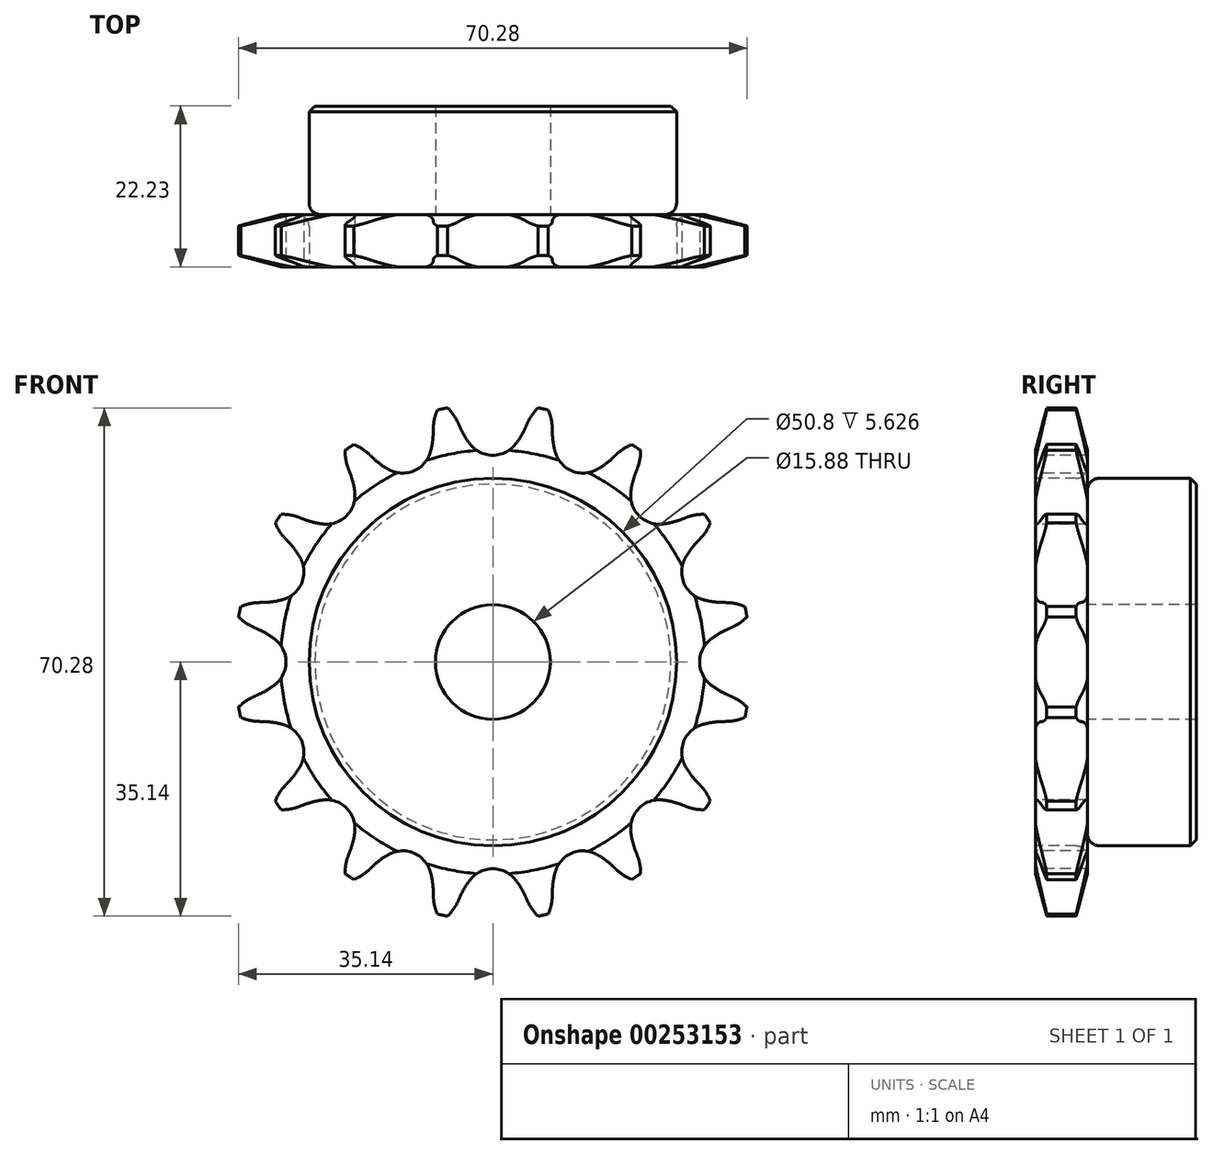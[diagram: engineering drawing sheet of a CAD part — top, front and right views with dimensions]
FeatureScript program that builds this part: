
annotation { "Feature Type Name" : "Feature", "Feature Type Description" : "" }
export const myFeature = defineFeature(function(context is Context, id is Id, definition is map)
    precondition{}
    {
        {
            var Q0;
            Q0=qCreatedBy(makeId("Right.planeOp"),FACE);
            var sketch = newSketch(context, id + "F0", { "sketchPlane" : qUnion([Q0])});
            skLineSegment(sketch, "E0", {"start": v(0, 0) * mm, "end": v(22.23, 0) * mm, "construction": true});
            skLineSegment(sketch, "E1.bottom", {"start": v(0, 7.94) * mm, "end": v(7.21, 7.94) * mm});
            skLineSegment(sketch, "E1.top", {"start": v(0, 35.69) * mm, "end": v(7.21, 35.69) * mm});
            skLineSegment(sketch, "E1.left", {"start": v(0, 7.94) * mm, "end": v(0, 35.69) * mm});
            skLineSegment(sketch, "E1.right", {"start": v(7.21, 7.94) * mm, "end": v(7.21, 35.69) * mm});
            skLineSegment(sketch, "E2.bottom", {"start": v(0, 7.94) * mm, "end": v(22.23, 7.94) * mm});
            skLineSegment(sketch, "E2.top", {"start": v(0, 25.4) * mm, "end": v(22.23, 25.4) * mm});
            skLineSegment(sketch, "E2.left", {"start": v(0, 7.94) * mm, "end": v(0, 25.4) * mm});
            skLineSegment(sketch, "E2.right", {"start": v(22.23, 7.94) * mm, "end": v(22.23, 25.4) * mm});
            skLineSegment(sketch, "E3.MirrorCS", {"start": v(0, -7.94) * mm, "end": v(7.21, -7.94) * mm});
            skLineSegment(sketch, "E4.MirrorCS", {"start": v(22.23, -7.94) * mm, "end": v(22.23, -25.4) * mm});
            skLineSegment(sketch, "E5.MirrorCS", {"start": v(0, -7.94) * mm, "end": v(0, -25.4) * mm});
            skLineSegment(sketch, "E6.MirrorCS", {"start": v(0, -35.69) * mm, "end": v(7.21, -35.69) * mm});
            skLineSegment(sketch, "E7.MirrorCS", {"start": v(0, -7.94) * mm, "end": v(0, -35.69) * mm});
            skLineSegment(sketch, "E8.MirrorCS", {"start": v(7.21, -7.94) * mm, "end": v(7.21, -35.69) * mm});
            skLineSegment(sketch, "E9.MirrorCS", {"start": v(0, -7.94) * mm, "end": v(22.23, -7.94) * mm});
            skLineSegment(sketch, "E10.MirrorCS", {"start": v(0, -25.4) * mm, "end": v(22.23, -25.4) * mm});
            skSolve(sketch);
        }
        {
            var Q0;
            {var subQ5=sQuery(id+"F0.wireOp",EDGE,"E2.right");Q0=makeQuery(id+"F0.imprint","IMPRINT",FACE,{"disambiguationData":[TD([[makeQuery(id+"F0.imprint","IMPRINT",EDGE,{"derivedFrom":subQ5}),1.0]])]});}
            var Q1;
            {var subQ5=sQuery(id+"F0.wireOp",EDGE,"E2.left");Q1=makeQuery(id+"F0.imprint","IMPRINT",FACE,{"disambiguationData":[TD([[makeQuery(id+"F0.imprint","IMPRINT",EDGE,{"derivedFrom":subQ5}),-1.0]])]});}
            var Q2;
            {var subQ0=sQuery(id+"F0.wireOp",EDGE,"E1.top");Q2=makeQuery(id+"F0.imprint","IMPRINT",FACE,{"disambiguationData":[TD([[makeQuery(id+"F0.imprint","IMPRINT",EDGE,{"derivedFrom":subQ0}),-1.0]])]});}
            var Q3;
            Q3=sQuery(id+"F0.wireOp",EDGE,"E0");
            revolve(context, id + "F1", {"entities" : qUnion([Q0, Q1, Q2]), "axis" : qUnion([Q3]), "revolveType" : RevolveType.FULL});
        }
        {
            var Q0;
            Q0=makeQuery(id+"F1.opRevolve","SWEPT_EDGE",EDGE,{"disambiguationData":[OSD([sQuery(id+"F0.wireOp",EDGE,"E1.right"),sQuery(id+"F0.wireOp",EDGE,"E2.top")])]});
            fillet(context, id + "F2", {"entities" : qUnion([Q0]), "radius" : 1.59 * mm, "tangentPropagation" : true, "allowEdgeOverflow" : false});
        }
        {
            var Q0;
            Q0=makeQuery(id+"F1.opRevolve","SWEPT_EDGE",EDGE,{"disambiguationData":[OSD([sQuery(id+"F0.wireOp",EDGE,"E2.top"),sQuery(id+"F0.wireOp",EDGE,"E2.right")])]});
            chamfer(context, id + "F3", {"entities" : qUnion([Q0]), "width" : 0.8 * mm, "tangentPropagation" : true});
        }
        {
            var Q0;
            Q0=makeQuery(id+"F1.opRevolve","SWEPT_EDGE",EDGE,{"disambiguationData":[OSD([sQuery(id+"F0.wireOp",EDGE,"E1.top"),sQuery(id+"F0.wireOp",EDGE,"E1.left")])]});
            var Q1;
            Q1=makeQuery(id+"F1.opRevolve","SWEPT_EDGE",EDGE,{"disambiguationData":[OSD([sQuery(id+"F0.wireOp",EDGE,"E1.top"),sQuery(id+"F0.wireOp",EDGE,"E1.right")])]});
            chamfer(context, id + "F4", {"entities" : qUnion([Q0, Q1]), "chamferType" : ChamferType.TWO_OFFSETS, "width1" : 6.35 * mm, "oppositeDirection" : false, "width2" : 1.57 * mm, "tangentPropagation" : true});
        }
        {
            var Q0;
            Q0=qCreatedBy(makeId("Front.planeOp"),FACE);
            var sketch = newSketch(context, id + "F5", { "sketchPlane" : qUnion([Q0])});
            skCircle(sketch, "E11", {"center": v(0, 0) * mm, "radius": 32.55 * mm, "construction": true});
            skLineSegment(sketch, "E12", {"start": v(0, 0) * mm, "end": v(0, 32.55) * mm, "construction": true});
            skLineSegment(sketch, "E13", {"start": v(29.08, 32.55) * mm, "end": v(0, 32.55) * mm, "construction": true});
            skLineSegment(sketch, "E14", {"start": v(0, 32.55) * mm, "end": v(5, 36.56) * mm, "construction": true});
            skLineSegment(sketch, "E15", {"start": v(5, 36.56) * mm, "end": v(-4.46, 32.3) * mm, "construction": true});
            skLineSegment(sketch, "E16", {"start": v(3.63, 14.35) * mm, "end": v(-4.46, 32.3) * mm, "construction": true});
            skLineSegment(sketch, "E17", {"start": v(0, 0) * mm, "end": v(-7.13, 35.85) * mm, "construction": true});
            skArc(sketch, "E18", {"start": v(-7.13, 35.85) * mm, "mid": v(-15.87, 26.15) * mm, "end": v(-4.82, 33.1) * mm, "construction": true});
            skArc(sketch, "E19", {"start": v(-4.82, 33.1) * mm, "mid": v(-5.78, 34.63) * mm, "end": v(-7.13, 35.85) * mm});
            skArc(sketch, "E20", {"start": v(-4.46, 32.3) * mm, "mid": v(-3.84, 31.14) * mm, "end": v(-3.1, 30.07) * mm});
            skLineSegment(sketch, "E21", {"start": v(-3.1, 30.07) * mm, "end": v(-3.1, 30.07) * mm});
            skArc(sketch, "E22.MirrorCS", {"start": v(4.46, 32.3) * mm, "mid": v(3.84, 31.14) * mm, "end": v(3.1, 30.07) * mm});
            skArc(sketch, "E23.MirrorCS", {"start": v(4.82, 33.1) * mm, "mid": v(5.78, 34.63) * mm, "end": v(7.13, 35.85) * mm});
            skLineSegment(sketch, "E24", {"start": v(4.82, 33.1) * mm, "end": v(4.46, 32.3) * mm});
            skLineSegment(sketch, "E25", {"start": v(3.1, 30.07) * mm, "end": v(3.1, 30.07) * mm});
            skArc(sketch, "E26", {"start": v(-3.1, 30.07) * mm, "mid": v(13.83, 41.97) * mm, "end": v(-4.46, 32.3) * mm, "construction": true});
            skArc(sketch, "E27", {"start": v(3.1, 30.07) * mm, "mid": v(0, 36.51) * mm, "end": v(-3.1, 30.07) * mm, "construction": true});
            skArc(sketch, "E28", {"start": v(-3.1, 30.07) * mm, "mid": v(0, 28.59) * mm, "end": v(3.1, 30.07) * mm});
            skLineSegment(sketch, "E29", {"start": v(-4.82, 33.1) * mm, "end": v(-4.46, 32.3) * mm});
            skArc(sketch, "E30.1.0", {"start": v(-17.12, 28.74) * mm, "mid": v(-18.6, 29.79) * mm, "end": v(-20.3, 30.4) * mm});
            skArc(sketch, "E30.1.1", {"start": v(-16.48, 28.14) * mm, "mid": v(-15.47, 27.3) * mm, "end": v(-14.36, 26.6) * mm});
            skArc(sketch, "E30.1.2", {"start": v(-14.36, 26.6) * mm, "mid": v(-10.94, 26.41) * mm, "end": v(-8.65, 28.96) * mm});
            skArc(sketch, "E30.1.3", {"start": v(-8.24, 31.55) * mm, "mid": v(-8.37, 30.24) * mm, "end": v(-8.65, 28.96) * mm});
            skLineSegment(sketch, "E30.1.4", {"start": v(-8.22, 32.42) * mm, "end": v(-8.24, 31.55) * mm});
            skArc(sketch, "E30.1.5", {"start": v(-8.22, 32.42) * mm, "mid": v(-7.91, 34.21) * mm, "end": v(-7.13, 35.85) * mm});
            skLineSegment(sketch, "E30.1.6", {"start": v(-17.12, 28.74) * mm, "end": v(-16.48, 28.14) * mm});
            skArc(sketch, "E30.2.0", {"start": v(-26.8, 20) * mm, "mid": v(-28.58, 20.4) * mm, "end": v(-30.4, 20.3) * mm});
            skArc(sketch, "E30.2.1", {"start": v(-26, 19.69) * mm, "mid": v(-24.74, 19.3) * mm, "end": v(-23.45, 19.08) * mm});
            skArc(sketch, "E30.2.2", {"start": v(-23.45, 19.08) * mm, "mid": v(-20.21, 20.21) * mm, "end": v(-19.08, 23.45) * mm});
            skArc(sketch, "E30.2.3", {"start": v(-19.69, 26) * mm, "mid": v(-19.3, 24.74) * mm, "end": v(-19.08, 23.45) * mm});
            skLineSegment(sketch, "E30.2.4", {"start": v(-20, 26.8) * mm, "end": v(-19.69, 26) * mm});
            skArc(sketch, "E30.2.5", {"start": v(-20, 26.8) * mm, "mid": v(-20.4, 28.58) * mm, "end": v(-20.3, 30.4) * mm});
            skLineSegment(sketch, "E30.2.6", {"start": v(-26.8, 20) * mm, "end": v(-26, 19.69) * mm});
            skArc(sketch, "E30.3.0", {"start": v(-32.42, 8.22) * mm, "mid": v(-34.21, 7.91) * mm, "end": v(-35.85, 7.13) * mm});
            skArc(sketch, "E30.3.1", {"start": v(-31.55, 8.24) * mm, "mid": v(-30.24, 8.37) * mm, "end": v(-28.96, 8.65) * mm});
            skArc(sketch, "E30.3.2", {"start": v(-28.96, 8.65) * mm, "mid": v(-26.41, 10.94) * mm, "end": v(-26.6, 14.36) * mm});
            skArc(sketch, "E30.3.3", {"start": v(-28.14, 16.48) * mm, "mid": v(-27.3, 15.47) * mm, "end": v(-26.6, 14.36) * mm});
            skLineSegment(sketch, "E30.3.4", {"start": v(-28.74, 17.12) * mm, "end": v(-28.14, 16.48) * mm});
            skArc(sketch, "E30.3.5", {"start": v(-28.74, 17.12) * mm, "mid": v(-29.79, 18.6) * mm, "end": v(-30.4, 20.3) * mm});
            skLineSegment(sketch, "E30.3.6", {"start": v(-32.42, 8.22) * mm, "end": v(-31.55, 8.24) * mm});
            skArc(sketch, "E30.4.0", {"start": v(-33.1, -4.82) * mm, "mid": v(-34.63, -5.78) * mm, "end": v(-35.85, -7.13) * mm});
            skArc(sketch, "E30.4.1", {"start": v(-32.3, -4.46) * mm, "mid": v(-31.14, -3.84) * mm, "end": v(-30.07, -3.1) * mm});
            skArc(sketch, "E30.4.2", {"start": v(-30.07, -3.1) * mm, "mid": v(-28.59, 0) * mm, "end": v(-30.07, 3.1) * mm});
            skArc(sketch, "E30.4.3", {"start": v(-32.3, 4.46) * mm, "mid": v(-31.14, 3.84) * mm, "end": v(-30.07, 3.1) * mm});
            skLineSegment(sketch, "E30.4.4", {"start": v(-33.1, 4.82) * mm, "end": v(-32.3, 4.46) * mm});
            skArc(sketch, "E30.4.5", {"start": v(-33.1, 4.82) * mm, "mid": v(-34.63, 5.78) * mm, "end": v(-35.85, 7.13) * mm});
            skLineSegment(sketch, "E30.4.6", {"start": v(-33.1, -4.82) * mm, "end": v(-32.3, -4.46) * mm});
            skArc(sketch, "E30.5.0", {"start": v(-28.74, -17.12) * mm, "mid": v(-29.79, -18.6) * mm, "end": v(-30.4, -20.3) * mm});
            skArc(sketch, "E30.5.1", {"start": v(-28.14, -16.48) * mm, "mid": v(-27.3, -15.47) * mm, "end": v(-26.6, -14.36) * mm});
            skArc(sketch, "E30.5.2", {"start": v(-26.6, -14.36) * mm, "mid": v(-26.41, -10.94) * mm, "end": v(-28.96, -8.65) * mm});
            skArc(sketch, "E30.5.3", {"start": v(-31.55, -8.24) * mm, "mid": v(-30.24, -8.37) * mm, "end": v(-28.96, -8.65) * mm});
            skLineSegment(sketch, "E30.5.4", {"start": v(-32.42, -8.22) * mm, "end": v(-31.55, -8.24) * mm});
            skArc(sketch, "E30.5.5", {"start": v(-32.42, -8.22) * mm, "mid": v(-34.21, -7.91) * mm, "end": v(-35.85, -7.13) * mm});
            skLineSegment(sketch, "E30.5.6", {"start": v(-28.74, -17.12) * mm, "end": v(-28.14, -16.48) * mm});
            skArc(sketch, "E30.6.0", {"start": v(-20, -26.8) * mm, "mid": v(-20.4, -28.58) * mm, "end": v(-20.3, -30.4) * mm});
            skArc(sketch, "E30.6.1", {"start": v(-19.69, -26) * mm, "mid": v(-19.3, -24.74) * mm, "end": v(-19.08, -23.45) * mm});
            skArc(sketch, "E30.6.2", {"start": v(-19.08, -23.45) * mm, "mid": v(-20.21, -20.21) * mm, "end": v(-23.45, -19.08) * mm});
            skArc(sketch, "E30.6.3", {"start": v(-26, -19.69) * mm, "mid": v(-24.74, -19.3) * mm, "end": v(-23.45, -19.08) * mm});
            skLineSegment(sketch, "E30.6.4", {"start": v(-26.8, -20) * mm, "end": v(-26, -19.69) * mm});
            skArc(sketch, "E30.6.5", {"start": v(-26.8, -20) * mm, "mid": v(-28.58, -20.4) * mm, "end": v(-30.4, -20.3) * mm});
            skLineSegment(sketch, "E30.6.6", {"start": v(-20, -26.8) * mm, "end": v(-19.69, -26) * mm});
            skArc(sketch, "E30.7.0", {"start": v(-8.22, -32.42) * mm, "mid": v(-7.91, -34.21) * mm, "end": v(-7.13, -35.85) * mm});
            skArc(sketch, "E30.7.1", {"start": v(-8.24, -31.55) * mm, "mid": v(-8.37, -30.24) * mm, "end": v(-8.65, -28.96) * mm});
            skArc(sketch, "E30.7.2", {"start": v(-8.65, -28.96) * mm, "mid": v(-10.94, -26.41) * mm, "end": v(-14.36, -26.6) * mm});
            skArc(sketch, "E30.7.3", {"start": v(-16.48, -28.14) * mm, "mid": v(-15.47, -27.3) * mm, "end": v(-14.36, -26.6) * mm});
            skLineSegment(sketch, "E30.7.4", {"start": v(-17.12, -28.74) * mm, "end": v(-16.48, -28.14) * mm});
            skArc(sketch, "E30.7.5", {"start": v(-17.12, -28.74) * mm, "mid": v(-18.6, -29.79) * mm, "end": v(-20.3, -30.4) * mm});
            skLineSegment(sketch, "E30.7.6", {"start": v(-8.22, -32.42) * mm, "end": v(-8.24, -31.55) * mm});
            skArc(sketch, "E30.8.0", {"start": v(4.82, -33.1) * mm, "mid": v(5.78, -34.63) * mm, "end": v(7.13, -35.85) * mm});
            skArc(sketch, "E30.8.1", {"start": v(4.46, -32.3) * mm, "mid": v(3.84, -31.14) * mm, "end": v(3.1, -30.07) * mm});
            skArc(sketch, "E30.8.2", {"start": v(3.1, -30.07) * mm, "mid": v(0, -28.59) * mm, "end": v(-3.1, -30.07) * mm});
            skArc(sketch, "E30.8.3", {"start": v(-4.46, -32.3) * mm, "mid": v(-3.84, -31.14) * mm, "end": v(-3.1, -30.07) * mm});
            skLineSegment(sketch, "E30.8.4", {"start": v(-4.82, -33.1) * mm, "end": v(-4.46, -32.3) * mm});
            skArc(sketch, "E30.8.5", {"start": v(-4.82, -33.1) * mm, "mid": v(-5.78, -34.63) * mm, "end": v(-7.13, -35.85) * mm});
            skLineSegment(sketch, "E30.8.6", {"start": v(4.82, -33.1) * mm, "end": v(4.46, -32.3) * mm});
            skArc(sketch, "E30.9.0", {"start": v(17.12, -28.74) * mm, "mid": v(18.6, -29.79) * mm, "end": v(20.3, -30.4) * mm});
            skArc(sketch, "E30.9.1", {"start": v(16.48, -28.14) * mm, "mid": v(15.47, -27.3) * mm, "end": v(14.36, -26.6) * mm});
            skArc(sketch, "E30.9.2", {"start": v(14.36, -26.6) * mm, "mid": v(10.94, -26.41) * mm, "end": v(8.65, -28.96) * mm});
            skArc(sketch, "E30.9.3", {"start": v(8.24, -31.55) * mm, "mid": v(8.37, -30.24) * mm, "end": v(8.65, -28.96) * mm});
            skLineSegment(sketch, "E30.9.4", {"start": v(8.22, -32.42) * mm, "end": v(8.24, -31.55) * mm});
            skArc(sketch, "E30.9.5", {"start": v(8.22, -32.42) * mm, "mid": v(7.91, -34.21) * mm, "end": v(7.13, -35.85) * mm});
            skLineSegment(sketch, "E30.9.6", {"start": v(17.12, -28.74) * mm, "end": v(16.48, -28.14) * mm});
            skArc(sketch, "E30.10.0", {"start": v(26.8, -20) * mm, "mid": v(28.58, -20.4) * mm, "end": v(30.4, -20.3) * mm});
            skArc(sketch, "E30.10.1", {"start": v(26, -19.69) * mm, "mid": v(24.74, -19.3) * mm, "end": v(23.45, -19.08) * mm});
            skArc(sketch, "E30.10.2", {"start": v(23.45, -19.08) * mm, "mid": v(20.21, -20.21) * mm, "end": v(19.08, -23.45) * mm});
            skArc(sketch, "E30.10.3", {"start": v(19.69, -26) * mm, "mid": v(19.3, -24.74) * mm, "end": v(19.08, -23.45) * mm});
            skLineSegment(sketch, "E30.10.4", {"start": v(20, -26.8) * mm, "end": v(19.69, -26) * mm});
            skArc(sketch, "E30.10.5", {"start": v(20, -26.8) * mm, "mid": v(20.4, -28.58) * mm, "end": v(20.3, -30.4) * mm});
            skLineSegment(sketch, "E30.10.6", {"start": v(26.8, -20) * mm, "end": v(26, -19.69) * mm});
            skArc(sketch, "E30.11.0", {"start": v(32.42, -8.22) * mm, "mid": v(34.21, -7.91) * mm, "end": v(35.85, -7.13) * mm});
            skArc(sketch, "E30.11.1", {"start": v(31.55, -8.24) * mm, "mid": v(30.24, -8.37) * mm, "end": v(28.96, -8.65) * mm});
            skArc(sketch, "E30.11.2", {"start": v(28.96, -8.65) * mm, "mid": v(26.41, -10.94) * mm, "end": v(26.6, -14.36) * mm});
            skArc(sketch, "E30.11.3", {"start": v(28.14, -16.48) * mm, "mid": v(27.3, -15.47) * mm, "end": v(26.6, -14.36) * mm});
            skLineSegment(sketch, "E30.11.4", {"start": v(28.74, -17.12) * mm, "end": v(28.14, -16.48) * mm});
            skArc(sketch, "E30.11.5", {"start": v(28.74, -17.12) * mm, "mid": v(29.79, -18.6) * mm, "end": v(30.4, -20.3) * mm});
            skLineSegment(sketch, "E30.11.6", {"start": v(32.42, -8.22) * mm, "end": v(31.55, -8.24) * mm});
            skArc(sketch, "E30.12.0", {"start": v(33.1, 4.82) * mm, "mid": v(34.63, 5.78) * mm, "end": v(35.85, 7.13) * mm});
            skArc(sketch, "E30.12.1", {"start": v(32.3, 4.46) * mm, "mid": v(31.14, 3.84) * mm, "end": v(30.07, 3.1) * mm});
            skArc(sketch, "E30.12.2", {"start": v(30.07, 3.1) * mm, "mid": v(28.59, 0) * mm, "end": v(30.07, -3.1) * mm});
            skArc(sketch, "E30.12.3", {"start": v(32.3, -4.46) * mm, "mid": v(31.14, -3.84) * mm, "end": v(30.07, -3.1) * mm});
            skLineSegment(sketch, "E30.12.4", {"start": v(33.1, -4.82) * mm, "end": v(32.3, -4.46) * mm});
            skArc(sketch, "E30.12.5", {"start": v(33.1, -4.82) * mm, "mid": v(34.63, -5.78) * mm, "end": v(35.85, -7.13) * mm});
            skLineSegment(sketch, "E30.12.6", {"start": v(33.1, 4.82) * mm, "end": v(32.3, 4.46) * mm});
            skArc(sketch, "E30.13.0", {"start": v(28.74, 17.12) * mm, "mid": v(29.79, 18.6) * mm, "end": v(30.4, 20.3) * mm});
            skArc(sketch, "E30.13.1", {"start": v(28.14, 16.48) * mm, "mid": v(27.3, 15.47) * mm, "end": v(26.6, 14.36) * mm});
            skArc(sketch, "E30.13.2", {"start": v(26.6, 14.36) * mm, "mid": v(26.41, 10.94) * mm, "end": v(28.96, 8.65) * mm});
            skArc(sketch, "E30.13.3", {"start": v(31.55, 8.24) * mm, "mid": v(30.24, 8.37) * mm, "end": v(28.96, 8.65) * mm});
            skLineSegment(sketch, "E30.13.4", {"start": v(32.42, 8.22) * mm, "end": v(31.55, 8.24) * mm});
            skArc(sketch, "E30.13.5", {"start": v(32.42, 8.22) * mm, "mid": v(34.21, 7.91) * mm, "end": v(35.85, 7.13) * mm});
            skLineSegment(sketch, "E30.13.6", {"start": v(28.74, 17.12) * mm, "end": v(28.14, 16.48) * mm});
            skArc(sketch, "E30.14.0", {"start": v(20, 26.8) * mm, "mid": v(20.4, 28.58) * mm, "end": v(20.3, 30.4) * mm});
            skArc(sketch, "E30.14.1", {"start": v(19.69, 26) * mm, "mid": v(19.3, 24.74) * mm, "end": v(19.08, 23.45) * mm});
            skArc(sketch, "E30.14.2", {"start": v(19.08, 23.45) * mm, "mid": v(20.21, 20.21) * mm, "end": v(23.45, 19.08) * mm});
            skArc(sketch, "E30.14.3", {"start": v(26, 19.69) * mm, "mid": v(24.74, 19.3) * mm, "end": v(23.45, 19.08) * mm});
            skLineSegment(sketch, "E30.14.4", {"start": v(26.8, 20) * mm, "end": v(26, 19.69) * mm});
            skArc(sketch, "E30.14.5", {"start": v(26.8, 20) * mm, "mid": v(28.58, 20.4) * mm, "end": v(30.4, 20.3) * mm});
            skLineSegment(sketch, "E30.14.6", {"start": v(20, 26.8) * mm, "end": v(19.69, 26) * mm});
            skArc(sketch, "E30.15.0", {"start": v(8.22, 32.42) * mm, "mid": v(7.91, 34.21) * mm, "end": v(7.13, 35.85) * mm});
            skArc(sketch, "E30.15.1", {"start": v(8.24, 31.55) * mm, "mid": v(8.37, 30.24) * mm, "end": v(8.65, 28.96) * mm});
            skArc(sketch, "E30.15.2", {"start": v(8.65, 28.96) * mm, "mid": v(10.94, 26.41) * mm, "end": v(14.36, 26.6) * mm});
            skArc(sketch, "E30.15.3", {"start": v(16.48, 28.14) * mm, "mid": v(15.47, 27.3) * mm, "end": v(14.36, 26.6) * mm});
            skLineSegment(sketch, "E30.15.4", {"start": v(17.12, 28.74) * mm, "end": v(16.48, 28.14) * mm});
            skArc(sketch, "E30.15.5", {"start": v(17.12, 28.74) * mm, "mid": v(18.6, 29.79) * mm, "end": v(20.3, 30.4) * mm});
            skLineSegment(sketch, "E30.15.6", {"start": v(8.22, 32.42) * mm, "end": v(8.24, 31.55) * mm});
            skSolve(sketch);
        }
        {
            var Q0;
            Q0 = qSketchRegion(id + "F5", true);
            extrude(context, id + "F6", {"entities" : qUnion([Q0]), "operationType" : NewBodyOperationType.INTERSECT, "endBound" : BoundingType.THROUGH_ALL, "oppositeDirection" : true, "depth" : 25.4 * mm});
        }
    });
